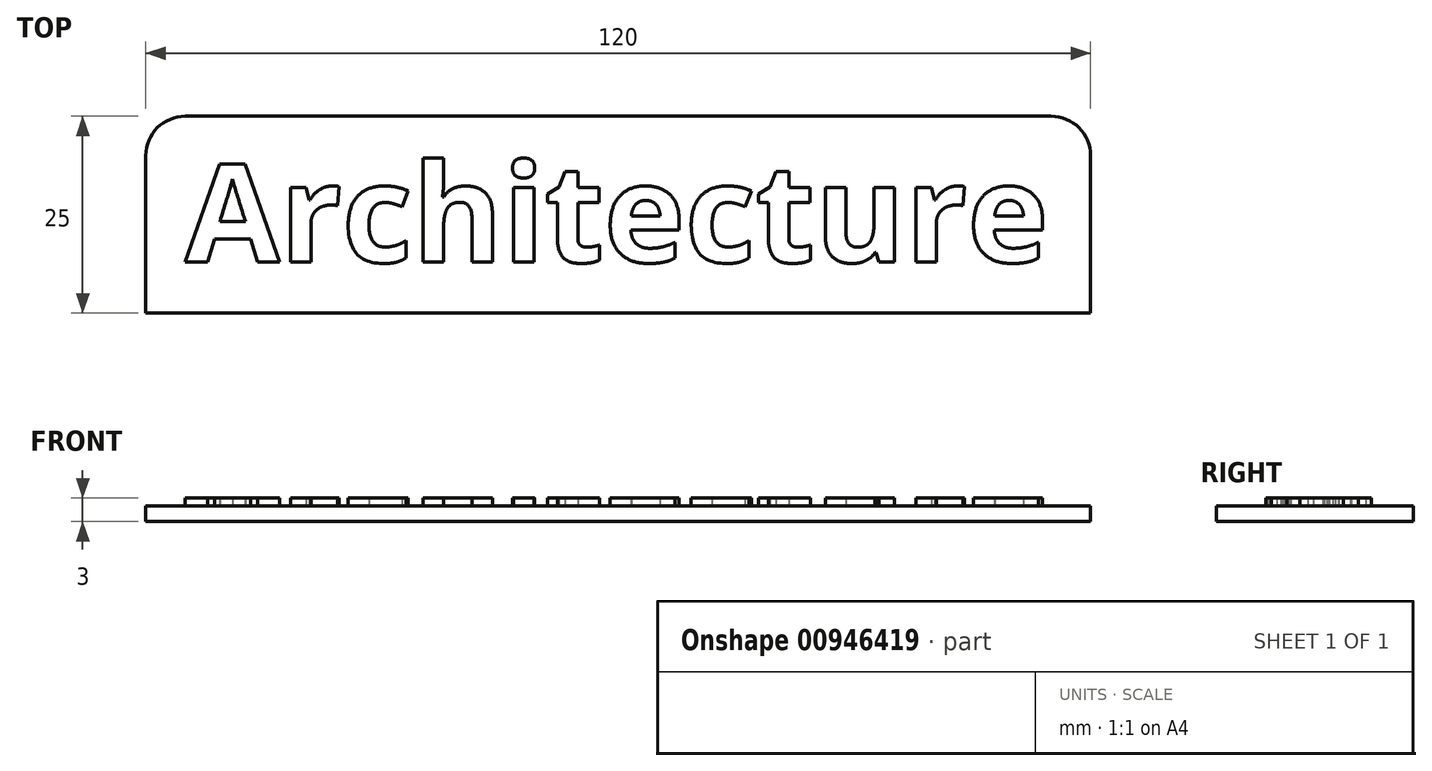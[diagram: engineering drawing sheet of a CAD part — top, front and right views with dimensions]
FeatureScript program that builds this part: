
annotation { "Feature Type Name" : "Feature", "Feature Type Description" : "" }
export const myFeature = defineFeature(function(context is Context, id is Id, definition is map)
    precondition{}
    {
        {
            var Q0;
            Q0=qCreatedBy(makeId("Top.planeOp"),FACE);
            var sketch = newSketch(context, id + "F0", { "sketchPlane" : qUnion([Q0])});
            skLineSegment(sketch, "E0.bottom", {"start": v(-60, 12.5) * mm, "end": v(60, 12.5) * mm});
            skLineSegment(sketch, "E0.top", {"start": v(-60, -12.5) * mm, "end": v(60, -12.5) * mm});
            skLineSegment(sketch, "E0.left", {"start": v(-60, 12.5) * mm, "end": v(-60, -12.5) * mm});
            skLineSegment(sketch, "E0.right", {"start": v(60, 12.5) * mm, "end": v(60, -12.5) * mm});
            skPoint(sketch, "E0.middle", {"position": v(0, 0) * mm});
            skSolve(sketch);
        }
        {
            var Q0;
            Q0=qSketchRegion(id+"F0",true);
            extrude(context, id + "F1", {"entities" : qUnion([Q0]), "depth" : 2 * mm, "offsetDistance" : 25 * mm});
        }
        {
            var Q0;
            Q0=makeQuery(id+"F1.opExtrude","CAP_FACE",FACE,{"disambiguationData":[OSD([sQuery(id+"F0.wireOp",EDGE,"E0.bottom"),sQuery(id+"F0.wireOp",EDGE,"E0.top"),sQuery(id+"F0.wireOp",EDGE,"E0.left"),sQuery(id+"F0.wireOp",EDGE,"E0.right")])],"isStart":false});
            var sketch = newSketch(context, id + "F2", { "sketchPlane" : qUnion([Q0])});
            skText(sketch, "E1", { "text": "Architecture\n", "fontName": "OpenSans-Bold.ttf"});
            const initialGuessF2  = {"E1": [-0.055, -0.00604, 1, 0, 0.01254]};
            skSetInitialGuess(sketch, initialGuessF2);
            skSolve(sketch);
        }
        {
            var Q0;
            Q0=qSketchRegion(id+"F2",true);
            extrude(context, id + "F3", {"entities" : qUnion([Q0]), "operationType" : NewBodyOperationType.ADD, "depth" : 1 * mm, "offsetDistance" : 25 * mm});
        }
        {
            var Q0;
            Q0=makeQuery(id+"F1.opExtrude","SWEPT_EDGE",EDGE,{"disambiguationData":[OSD([sQuery(id+"F0.wireOp",EDGE,"E0.bottom"),sQuery(id+"F0.wireOp",EDGE,"E0.left")])]});
            var Q1;
            Q1=makeQuery(id+"F1.opExtrude","SWEPT_EDGE",EDGE,{"disambiguationData":[OSD([sQuery(id+"F0.wireOp",EDGE,"E0.bottom"),sQuery(id+"F0.wireOp",EDGE,"E0.right")])]});
            fillet(context, id + "F4", {"entities" : qUnion([Q0, Q1]), "radius" : 5 * mm, "tangentPropagation" : true, "allowEdgeOverflow" : false});
        }
    });
